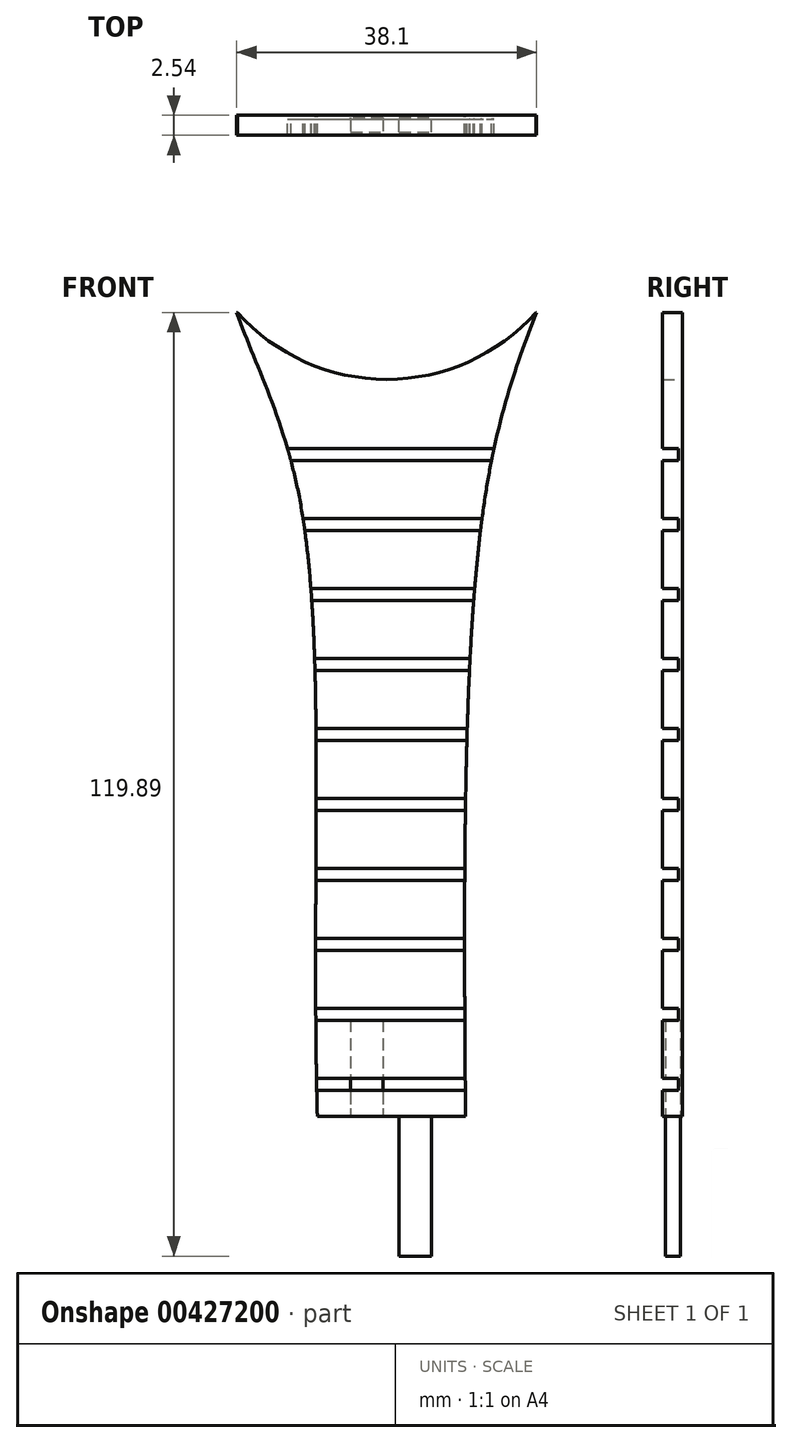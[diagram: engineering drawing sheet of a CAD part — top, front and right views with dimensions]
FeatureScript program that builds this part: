
annotation { "Feature Type Name" : "Feature", "Feature Type Description" : "" }
export const myFeature = defineFeature(function(context is Context, id is Id, definition is map)
    precondition{}
    {
        {
            var Q0;
            Q0=qCreatedBy(makeId("Front.planeOp"),FACE);
            var sketch = newSketch(context, id + "F0", { "sketchPlane" : qUnion([Q0])});
            skFitSpline(sketch, "E0", {"points": [v(-38.1, 45.5) * mm, v(-30.14, 21.94) * mm, v(-27.87, -56.6) * mm], "startDerivative": vector(19.18, -55.1) * mm, "endDerivative": vector(3.86, -149.3) * mm});
            skFitSpline(sketch, "E1", {"points": [v(0, 45.5) * mm, v(-6.58, 21.94) * mm, v(-9.05, -56.6) * mm], "startDerivative": vector(-21.64, -54.74) * mm, "endDerivative": vector(1.2, -149.86) * mm});
            skLineSegment(sketch, "E2", {"start": v(-27.87, -56.6) * mm, "end": v(-9.05, -56.6) * mm});
            skLineSegment(sketch, "E3", {"start": v(-38.1, 45.5) * mm, "end": v(0, 45.5) * mm});
            skFitSpline(sketch, "E4", {"points": [v(-38.1, 45.5) * mm, v(-18.45, 35.78) * mm, v(0, 45.5) * mm], "startDerivative": vector(39.18, -29.09) * mm, "endDerivative": vector(37.01, 29.33) * mm});
            skSolve(sketch);
        }
        {
            var Q0;
            Q0=qSketchRegion(id+"F0",true);
            extrude(context, id + "F1", {"entities" : qUnion([Q0]), "depth" : 2.54 * mm});
        }
        {
            var Q0;
            Q0=qCreatedBy(makeId("Front.planeOp"),FACE);
            var sketch = newSketch(context, id + "F2", { "sketchPlane" : qUnion([Q0])});
            skPoint(sketch, "E5.0", {"position": v(-19.05, 45.5) * mm});
            skCircle(sketch, "E6", {"center": v(-19.05, 62.4) * mm, "radius": 25.4 * mm});
            skSolve(sketch);
        }
        {
            var Q0;
            Q0=qSketchRegion(id+"F2",true);
            extrude(context, id + "F3", {"entities" : qUnion([Q0]), "operationType" : NewBodyOperationType.REMOVE, "depth" : 25.4 * mm});
        }
        {
            var Q0;
            Q0=makeQuery(id+"F1.opExtrude","CAP_FACE",FACE,{"disambiguationData":[OSD([sQuery(id+"F0.wireOp",EDGE,"E0"),sQuery(id+"F0.wireOp",EDGE,"E1"),sQuery(id+"F0.wireOp",EDGE,"E2"),sQuery(id+"F0.wireOp",EDGE,"E3")])],"isStart":false});
            var sketch = newSketch(context, id + "F4", { "sketchPlane" : qUnion([Q0])});
            skLineSegment(sketch, "E7.bottom", {"start": v(-38.95, 28.23) * mm, "end": v(2.15, 28.23) * mm});
            skLineSegment(sketch, "E7.top", {"start": v(-38.95, 26.7) * mm, "end": v(2.15, 26.7) * mm});
            skLineSegment(sketch, "E7.left", {"start": v(-38.95, 28.23) * mm, "end": v(-38.95, 26.7) * mm});
            skLineSegment(sketch, "E7.right", {"start": v(2.15, 28.23) * mm, "end": v(2.15, 26.7) * mm});
            skLineSegment(sketch, "E8.0.1.0", {"start": v(-38.95, 19.34) * mm, "end": v(2.15, 19.34) * mm});
            skLineSegment(sketch, "E8.0.1.1", {"start": v(2.15, 19.34) * mm, "end": v(2.15, 17.82) * mm});
            skLineSegment(sketch, "E8.0.1.2", {"start": v(-38.95, 17.82) * mm, "end": v(2.15, 17.82) * mm});
            skLineSegment(sketch, "E8.0.1.3", {"start": v(-38.95, 19.34) * mm, "end": v(-38.95, 17.82) * mm});
            skLineSegment(sketch, "E8.0.2.0", {"start": v(-38.95, 10.45) * mm, "end": v(2.15, 10.45) * mm});
            skLineSegment(sketch, "E8.0.2.1", {"start": v(2.15, 10.45) * mm, "end": v(2.15, 8.93) * mm});
            skLineSegment(sketch, "E8.0.2.2", {"start": v(-38.95, 8.93) * mm, "end": v(2.15, 8.93) * mm});
            skLineSegment(sketch, "E8.0.2.3", {"start": v(-38.95, 10.45) * mm, "end": v(-38.95, 8.93) * mm});
            skLineSegment(sketch, "E8.0.3.0", {"start": v(-38.95, 1.56) * mm, "end": v(2.15, 1.56) * mm});
            skLineSegment(sketch, "E8.0.3.1", {"start": v(2.15, 1.56) * mm, "end": v(2.15, 0.04) * mm});
            skLineSegment(sketch, "E8.0.3.2", {"start": v(-38.95, 0.04) * mm, "end": v(2.15, 0.04) * mm});
            skLineSegment(sketch, "E8.0.3.3", {"start": v(-38.95, 1.56) * mm, "end": v(-38.95, 0.04) * mm});
            skLineSegment(sketch, "E8.0.4.0", {"start": v(-38.95, -7.33) * mm, "end": v(2.15, -7.33) * mm});
            skLineSegment(sketch, "E8.0.4.1", {"start": v(2.15, -7.33) * mm, "end": v(2.15, -8.85) * mm});
            skLineSegment(sketch, "E8.0.4.2", {"start": v(-38.95, -8.85) * mm, "end": v(2.15, -8.85) * mm});
            skLineSegment(sketch, "E8.0.4.3", {"start": v(-38.95, -7.33) * mm, "end": v(-38.95, -8.85) * mm});
            skLineSegment(sketch, "E8.0.5.0", {"start": v(-38.95, -16.22) * mm, "end": v(2.15, -16.22) * mm});
            skLineSegment(sketch, "E8.0.5.1", {"start": v(2.15, -16.22) * mm, "end": v(2.15, -17.74) * mm});
            skLineSegment(sketch, "E8.0.5.2", {"start": v(-38.95, -17.74) * mm, "end": v(2.15, -17.74) * mm});
            skLineSegment(sketch, "E8.0.5.3", {"start": v(-38.95, -16.22) * mm, "end": v(-38.95, -17.74) * mm});
            skLineSegment(sketch, "E8.0.6.0", {"start": v(-38.95, -25.11) * mm, "end": v(2.15, -25.11) * mm});
            skLineSegment(sketch, "E8.0.6.1", {"start": v(2.15, -25.11) * mm, "end": v(2.15, -26.63) * mm});
            skLineSegment(sketch, "E8.0.6.2", {"start": v(-38.95, -26.63) * mm, "end": v(2.15, -26.63) * mm});
            skLineSegment(sketch, "E8.0.6.3", {"start": v(-38.95, -25.11) * mm, "end": v(-38.95, -26.63) * mm});
            skLineSegment(sketch, "E8.0.7.0", {"start": v(-38.95, -34) * mm, "end": v(2.15, -34) * mm});
            skLineSegment(sketch, "E8.0.7.1", {"start": v(2.15, -34) * mm, "end": v(2.15, -35.52) * mm});
            skLineSegment(sketch, "E8.0.7.2", {"start": v(-38.95, -35.52) * mm, "end": v(2.15, -35.52) * mm});
            skLineSegment(sketch, "E8.0.7.3", {"start": v(-38.95, -34) * mm, "end": v(-38.95, -35.52) * mm});
            skLineSegment(sketch, "E8.0.8.0", {"start": v(-38.95, -42.9) * mm, "end": v(2.15, -42.9) * mm});
            skLineSegment(sketch, "E8.0.8.1", {"start": v(2.15, -42.9) * mm, "end": v(2.15, -44.41) * mm});
            skLineSegment(sketch, "E8.0.8.2", {"start": v(-38.95, -44.41) * mm, "end": v(2.15, -44.41) * mm});
            skLineSegment(sketch, "E8.0.8.3", {"start": v(-38.95, -42.9) * mm, "end": v(-38.95, -44.41) * mm});
            skLineSegment(sketch, "E8.0.9.0", {"start": v(-38.95, -51.78) * mm, "end": v(2.15, -51.78) * mm});
            skLineSegment(sketch, "E8.0.9.1", {"start": v(2.15, -51.78) * mm, "end": v(2.15, -53.3) * mm});
            skLineSegment(sketch, "E8.0.9.2", {"start": v(-38.95, -53.3) * mm, "end": v(2.15, -53.3) * mm});
            skLineSegment(sketch, "E8.0.9.3", {"start": v(-38.95, -51.78) * mm, "end": v(-38.95, -53.3) * mm});
            skLineSegment(sketch, "E8.direction1", {"start": v(-38.95, 28.23) * mm, "end": v(-13.55, 28.23) * mm, "construction": true});
            skLineSegment(sketch, "E8.direction2", {"start": v(-38.95, 28.23) * mm, "end": v(-38.95, 19.34) * mm, "construction": true});
            skSolve(sketch);
        }
        {
            var Q0;
            Q0=qSketchRegion(id+"F4",true);
            extrude(context, id + "F5", {"entities" : qUnion([Q0]), "operationType" : NewBodyOperationType.REMOVE, "oppositeDirection" : true, "depth" : 2.03 * mm});
        }
        {
            var Q0;
            Q0=makeQuery(id+"F1.opExtrude","SWEPT_FACE",FACE,{"disambiguationData":[OSD([sQuery(id+"F0.wireOp",EDGE,"E2")])]});
            var sketch = newSketch(context, id + "F6", { "sketchPlane" : qUnion([Q0])});
            skLineSegment(sketch, "E9.bottom", {"start": v(-17.46, 2.16) * mm, "end": v(-13.37, 2.16) * mm});
            skLineSegment(sketch, "E9.top", {"start": v(-17.46, 0.27) * mm, "end": v(-13.37, 0.27) * mm});
            skLineSegment(sketch, "E9.left", {"start": v(-17.46, 2.16) * mm, "end": v(-17.46, 0.27) * mm});
            skLineSegment(sketch, "E9.right", {"start": v(-13.37, 2.16) * mm, "end": v(-13.37, 0.27) * mm});
            skLineSegment(sketch, "E10.MirrorCS", {"start": v(-19.46, 2.16) * mm, "end": v(-19.46, 0.27) * mm});
            skLineSegment(sketch, "E11.MirrorCS", {"start": v(-23.55, 2.16) * mm, "end": v(-23.55, 0.27) * mm});
            skLineSegment(sketch, "E12.MirrorCS", {"start": v(-19.45, 0.27) * mm, "end": v(-23.54, 0.27) * mm});
            skLineSegment(sketch, "E13", {"start": v(-23.55, 2.16) * mm, "end": v(-19.46, 2.16) * mm});
            skSolve(sketch);
        }
        {
            var Q0;
            Q0=makeQuery(id+"F6.imprint","IMPRINT",FACE,{"disambiguationData":[TD([[makeQuery(id+"F6.imprint","IMPRINT",EDGE,{"derivedFrom":sQuery(id+"F6.wireOp",EDGE,"E9.bottom")}),-1.0]])]});
            var Q1;
            Q1=makeQuery(id+"F5.boolean.opBoolean","COPY",FACE,{"derivedFrom":makeQuery(id+"F5.opExtrude","SWEPT_FACE",FACE,{"disambiguationData":[OSD([sQuery(id+"F4.wireOp",EDGE,"E8.0.8.2")])]})});
            extrude(context, id + "F7", {"entities" : qUnion([Q0]), "endBoundEntityFace" : qUnion([Q1]), "depth" : 17.78 * mm});
        }
        {
            var Q0;
            Q0=makeQuery(id+"F1.opExtrude","SWEPT_FACE",FACE,{"disambiguationData":[OSD([sQuery(id+"F0.wireOp",EDGE,"E2")])]});
            var sketch = newSketch(context, id + "F8", { "sketchPlane" : qUnion([Q0])});
            skLineSegment(sketch, "E14", {"start": v(-19.54, 0.28) * mm, "end": v(-23.63, 0.28) * mm});
            skLineSegment(sketch, "E15", {"start": v(-23.63, 0.28) * mm, "end": v(-23.63, 2.16) * mm});
            skLineSegment(sketch, "E16", {"start": v(-19.54, 0.28) * mm, "end": v(-19.54, 2.16) * mm});
            skLineSegment(sketch, "E17", {"start": v(-23.63, 2.16) * mm, "end": v(-19.54, 2.16) * mm});
            skSolve(sketch);
        }
        {
            var Q0;
            Q0 = qSketchRegion(id + "F8", true);
            var Q1;
            Q1=makeQuery(id+"F5.boolean.opBoolean","COPY",FACE,{"derivedFrom":makeQuery(id+"F5.opExtrude","SWEPT_FACE",FACE,{"disambiguationData":[OSD([sQuery(id+"F4.wireOp",EDGE,"E8.0.8.2")])]})});
            extrude(context, id + "F9", {"entities" : qUnion([Q0]), "operationType" : NewBodyOperationType.REMOVE, "endBound" : BoundingType.UP_TO_SURFACE, "oppositeDirection" : true, "endBoundEntityFace" : qUnion([Q1]), "depth" : 17.78 * mm});
        }
    });
